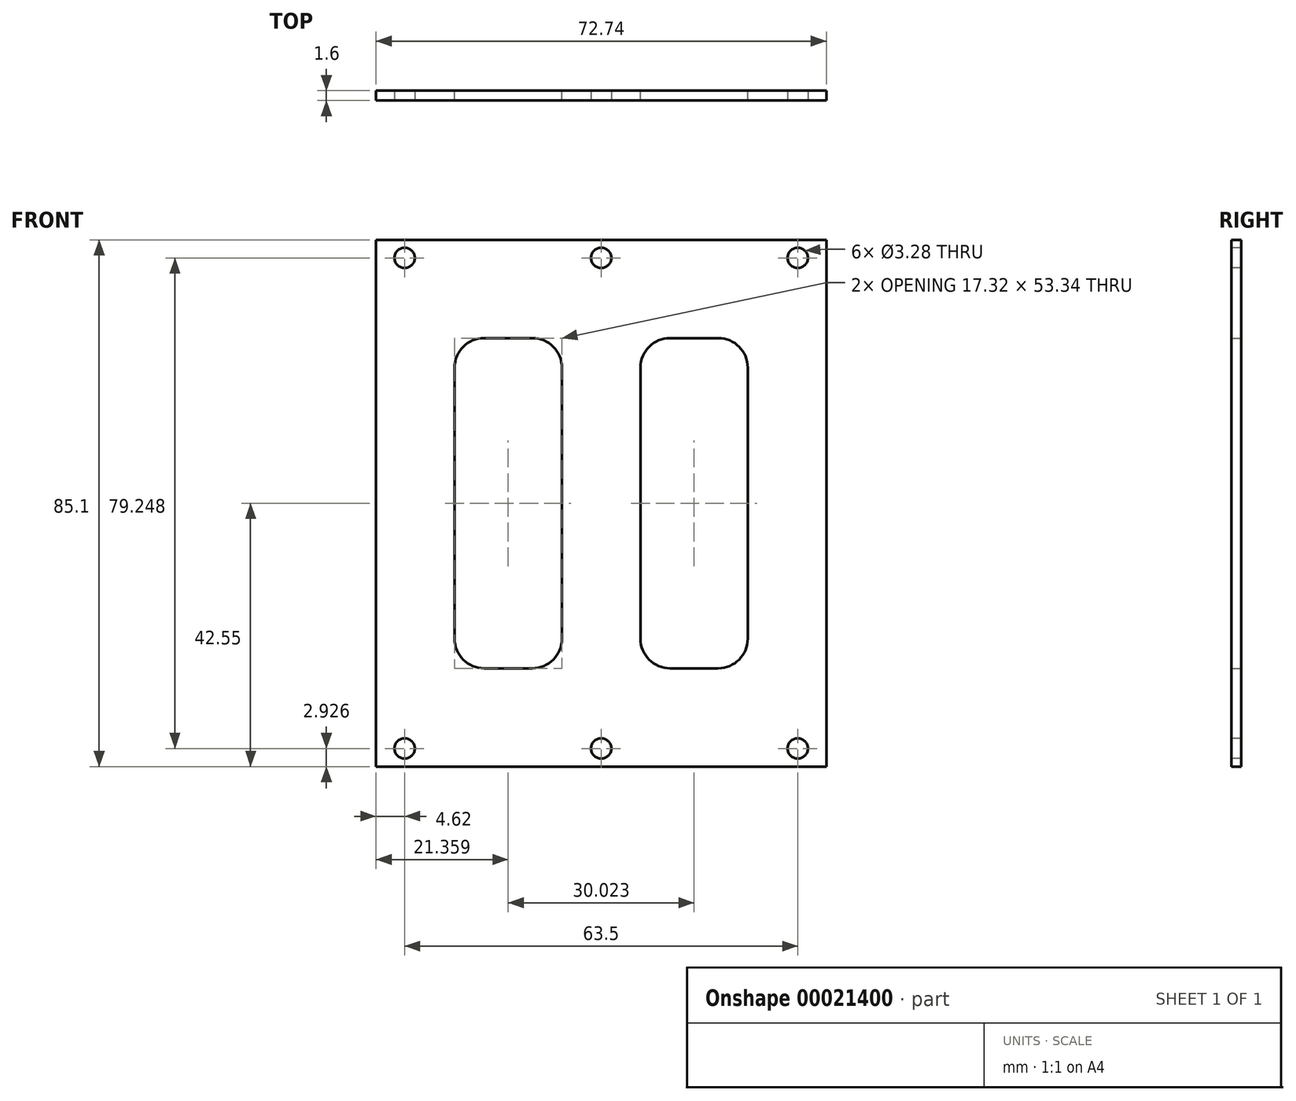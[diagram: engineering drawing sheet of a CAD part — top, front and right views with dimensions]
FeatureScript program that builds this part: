
annotation { "Feature Type Name" : "Feature", "Feature Type Description" : "" }
export const myFeature = defineFeature(function(context is Context, id is Id, definition is map)
    precondition{}
    {
        {
            var Q0;
            Q0=qCreatedBy(makeId("Front.planeOp"),FACE);
            var sketch = newSketch(context, id + "F0", { "sketchPlane" : qUnion([Q0])});
            skLineSegment(sketch, "E0.rect.bottom", {"start": v(36.37, -42.55) * mm, "end": v(-36.37, -42.55) * mm});
            skLineSegment(sketch, "E0.rect.top", {"start": v(36.37, 42.55) * mm, "end": v(-36.37, 42.55) * mm});
            skLineSegment(sketch, "E0.rect.left", {"start": v(36.37, -42.55) * mm, "end": v(36.37, 42.55) * mm});
            skLineSegment(sketch, "E0.rect.right", {"start": v(-36.37, -42.55) * mm, "end": v(-36.37, 42.55) * mm});
            skPoint(sketch, "E0.rect.middle", {"position": v(0, 0) * mm});
            skLineSegment(sketch, "E1.rect.bottom", {"start": v(-23.67, 26.67) * mm, "end": v(-6.35, 26.67) * mm});
            skLineSegment(sketch, "E1.rect.top", {"start": v(-23.67, -26.67) * mm, "end": v(-6.35, -26.67) * mm});
            skLineSegment(sketch, "E1.rect.left", {"start": v(-23.67, 26.67) * mm, "end": v(-23.67, -26.67) * mm});
            skLineSegment(sketch, "E1.rect.right", {"start": v(-6.35, 26.67) * mm, "end": v(-6.35, -26.67) * mm});
            skPoint(sketch, "E1.rect.middle", {"position": v(-15.01, 0) * mm});
            skLineSegment(sketch, "E2.rect.bottom", {"start": v(6.35, 26.67) * mm, "end": v(23.67, 26.67) * mm});
            skLineSegment(sketch, "E2.rect.top", {"start": v(6.35, -26.67) * mm, "end": v(23.67, -26.67) * mm});
            skLineSegment(sketch, "E2.rect.left", {"start": v(6.35, 26.67) * mm, "end": v(6.35, -26.67) * mm});
            skLineSegment(sketch, "E2.rect.right", {"start": v(23.67, 26.67) * mm, "end": v(23.67, -26.67) * mm});
            skPoint(sketch, "E2.rect.middle", {"position": v(15.01, 0) * mm});
            skSolve(sketch);
        }
        {
            var Q0;
            Q0=makeQuery(id+"F0.imprint","IMPRINT",FACE,{"disambiguationData":[TD([[makeQuery(id+"F0.imprint","IMPRINT",EDGE,{"derivedFrom":sQuery(id+"F0.wireOp",EDGE,"E0.rect.bottom")}),-1.0]])]});
            extrude(context, id + "F1", {"entities" : qUnion([Q0]), "depth" : 1.6 * mm});
        }
        {
            var Q0;
            Q0=makeQuery(id+"F1.opExtrude","SWEPT_EDGE",EDGE,{"disambiguationData":[OSD([sQuery(id+"F0.wireOp",EDGE,"E1.rect.bottom"),sQuery(id+"F0.wireOp",EDGE,"E1.rect.left")])]});
            var Q1;
            Q1=makeQuery(id+"F1.opExtrude","SWEPT_EDGE",EDGE,{"disambiguationData":[OSD([sQuery(id+"F0.wireOp",EDGE,"E2.rect.bottom"),sQuery(id+"F0.wireOp",EDGE,"E2.rect.left")])]});
            var Q2;
            Q2=makeQuery(id+"F1.opExtrude","SWEPT_EDGE",EDGE,{"disambiguationData":[OSD([sQuery(id+"F0.wireOp",EDGE,"E2.rect.bottom"),sQuery(id+"F0.wireOp",EDGE,"E2.rect.right")])]});
            var Q3;
            Q3=makeQuery(id+"F1.opExtrude","SWEPT_EDGE",EDGE,{"disambiguationData":[OSD([sQuery(id+"F0.wireOp",EDGE,"E1.rect.bottom"),sQuery(id+"F0.wireOp",EDGE,"E1.rect.right")])]});
            var Q4;
            Q4=makeQuery(id+"F1.opExtrude","SWEPT_EDGE",EDGE,{"disambiguationData":[OSD([sQuery(id+"F0.wireOp",EDGE,"E2.rect.top"),sQuery(id+"F0.wireOp",EDGE,"E2.rect.right")])]});
            var Q5;
            Q5=makeQuery(id+"F1.opExtrude","SWEPT_EDGE",EDGE,{"disambiguationData":[OSD([sQuery(id+"F0.wireOp",EDGE,"E2.rect.top"),sQuery(id+"F0.wireOp",EDGE,"E2.rect.left")])]});
            var Q6;
            Q6=makeQuery(id+"F1.opExtrude","SWEPT_EDGE",EDGE,{"disambiguationData":[OSD([sQuery(id+"F0.wireOp",EDGE,"E1.rect.top"),sQuery(id+"F0.wireOp",EDGE,"E1.rect.left")])]});
            var Q7;
            Q7=makeQuery(id+"F1.opExtrude","SWEPT_EDGE",EDGE,{"disambiguationData":[OSD([sQuery(id+"F0.wireOp",EDGE,"E1.rect.top"),sQuery(id+"F0.wireOp",EDGE,"E1.rect.right")])]});
            fillet(context, id + "F2", {"entities" : qUnion([Q0, Q1, Q2, Q3, Q4, Q5, Q6, Q7]), "radius" : 4.78 * mm, "tangentPropagation" : true, "allowEdgeOverflow" : false});
        }
        {
            var Q0;
            Q0=makeQuery(id+"F1.opExtrude","CAP_FACE",FACE,{"disambiguationData":[OSD([sQuery(id+"F0.wireOp",EDGE,"E0.rect.bottom"),sQuery(id+"F0.wireOp",EDGE,"E0.rect.top"),sQuery(id+"F0.wireOp",EDGE,"E0.rect.left"),sQuery(id+"F0.wireOp",EDGE,"E0.rect.right"),sQuery(id+"F0.wireOp",EDGE,"E1.rect.bottom"),sQuery(id+"F0.wireOp",EDGE,"E1.rect.top"),sQuery(id+"F0.wireOp",EDGE,"E1.rect.left"),sQuery(id+"F0.wireOp",EDGE,"E1.rect.right"),sQuery(id+"F0.wireOp",EDGE,"E2.rect.bottom"),sQuery(id+"F0.wireOp",EDGE,"E2.rect.top"),sQuery(id+"F0.wireOp",EDGE,"E2.rect.left"),sQuery(id+"F0.wireOp",EDGE,"E2.rect.right")])],"isStart":false});
            var sketch = newSketch(context, id + "F3", { "sketchPlane" : qUnion([Q0])});
            skLineSegment(sketch, "E3.rect.bottom", {"start": v(31.75, -39.62) * mm, "end": v(-31.75, -39.62) * mm});
            skLineSegment(sketch, "E3.rect.top", {"start": v(31.75, 39.62) * mm, "end": v(-31.75, 39.62) * mm});
            skLineSegment(sketch, "E3.rect.left", {"start": v(31.75, -39.62) * mm, "end": v(31.75, 39.62) * mm});
            skLineSegment(sketch, "E3.rect.right", {"start": v(-31.75, -39.62) * mm, "end": v(-31.75, 39.62) * mm});
            skPoint(sketch, "E3.rect.middle", {"position": v(0, 0) * mm});
            skLineSegment(sketch, "E4", {"start": v(0, 39.62) * mm, "end": v(0, -39.62) * mm});
            skSolve(sketch);
        }
        {
            var Q0;
            Q0=sQuery(id+"F3.wireOp",VERTEX,"E3.rect.right.end");
            var Q1;
            Q1=sQuery(id+"F3.wireOp",VERTEX,"E4.start");
            var Q2;
            Q2=sQuery(id+"F3.wireOp",VERTEX,"E3.rect.left.end");
            var Q3;
            Q3=sQuery(id+"F3.wireOp",VERTEX,"E3.rect.right.start");
            var Q4;
            Q4=sQuery(id+"F3.wireOp",VERTEX,"E4.end");
            var Q5;
            Q5=sQuery(id+"F3.wireOp",VERTEX,"E3.rect.bottom.start");
            var Q6;
            Q6=makeQuery(id+"F1.opExtrude","SWEPT_BODY",BODY,{"disambiguationData":[OSD([sQuery(id+"F0.wireOp",EDGE,"E0.rect.bottom"),sQuery(id+"F0.wireOp",EDGE,"E0.rect.top"),sQuery(id+"F0.wireOp",EDGE,"E0.rect.left"),sQuery(id+"F0.wireOp",EDGE,"E0.rect.right"),sQuery(id+"F0.wireOp",EDGE,"E1.rect.bottom"),sQuery(id+"F0.wireOp",EDGE,"E1.rect.top"),sQuery(id+"F0.wireOp",EDGE,"E1.rect.left"),sQuery(id+"F0.wireOp",EDGE,"E1.rect.right"),sQuery(id+"F0.wireOp",EDGE,"E2.rect.bottom"),sQuery(id+"F0.wireOp",EDGE,"E2.rect.top"),sQuery(id+"F0.wireOp",EDGE,"E2.rect.left"),sQuery(id+"F0.wireOp",EDGE,"E2.rect.right")])]});
            hole(context, id + "F4", {"style" : HoleStyle.SIMPLE, "holeDiameter" : 3.28 * mm, "endStyle" : HoleEndStyle.THROUGH, "locations" : qUnion([Q0, Q1, Q2, Q3, Q4, Q5]), "scope" : qUnion([Q6])});
        }
    });
